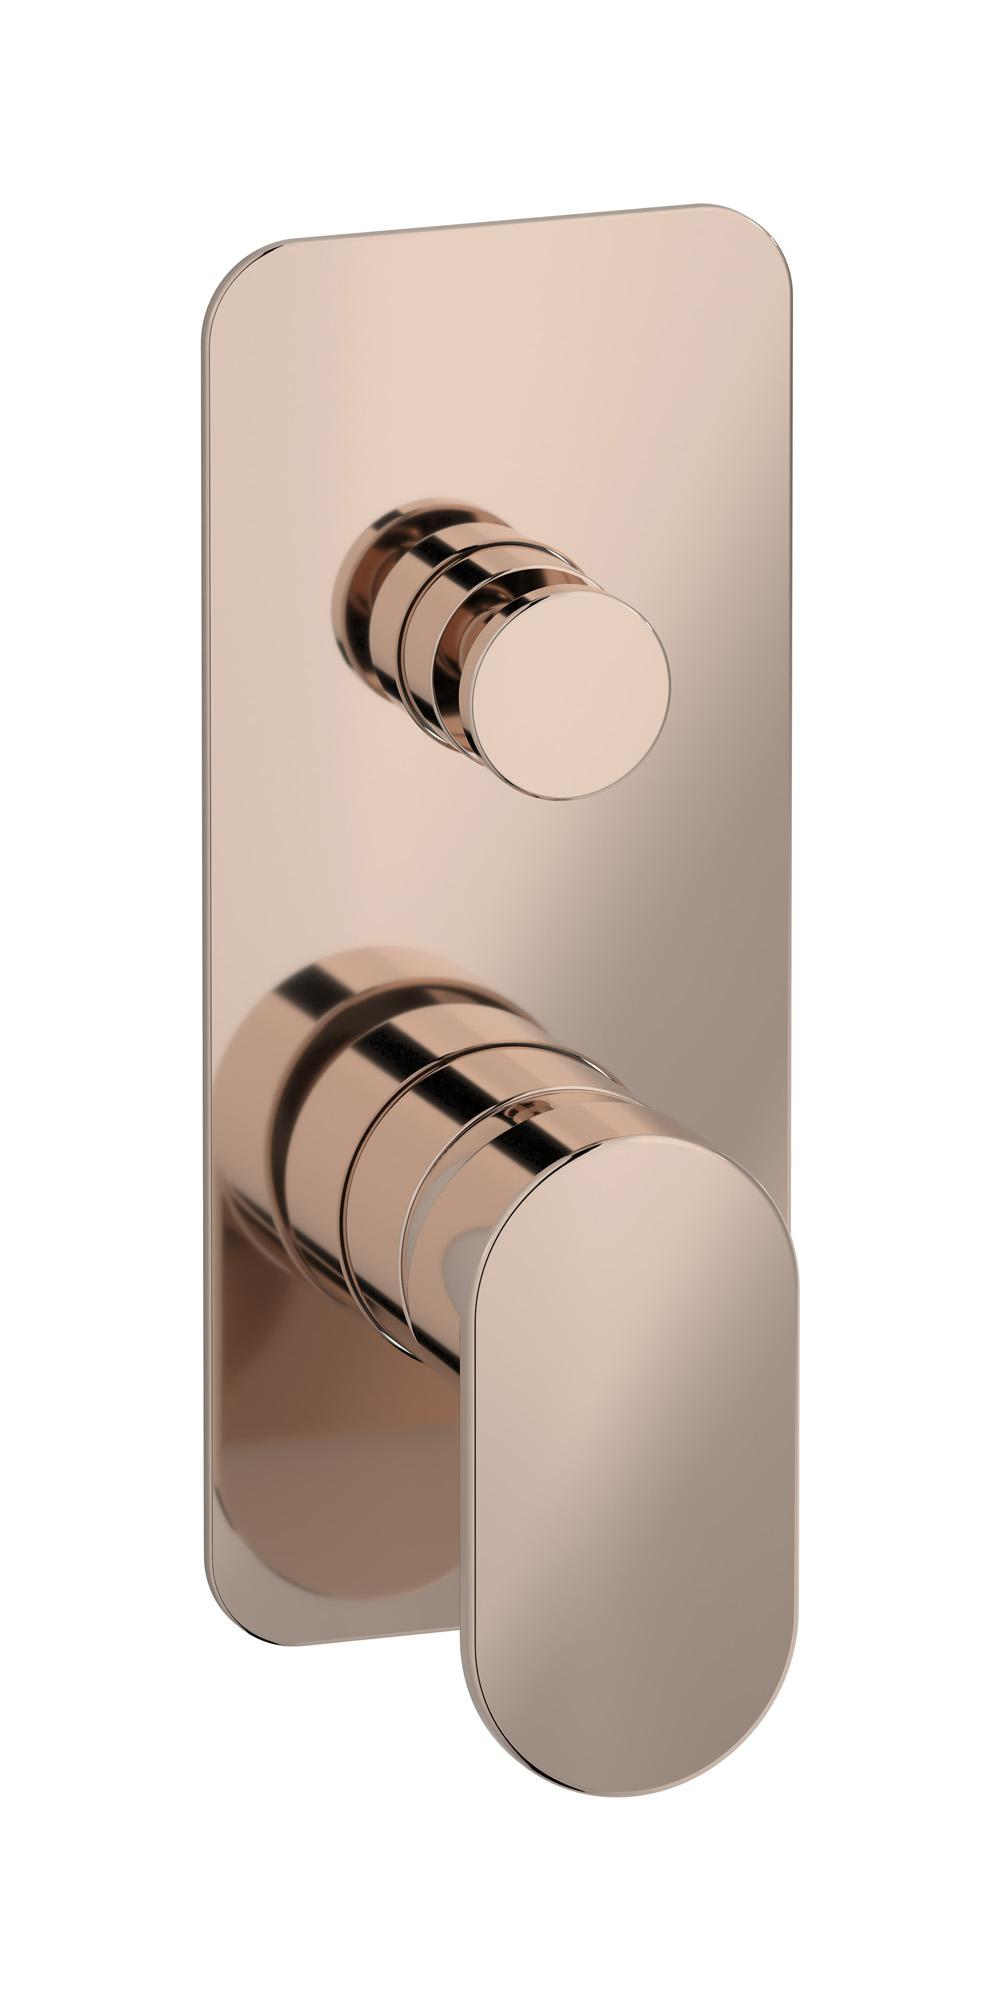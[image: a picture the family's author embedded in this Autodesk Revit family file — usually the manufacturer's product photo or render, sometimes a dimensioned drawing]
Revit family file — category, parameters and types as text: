
# Revit family: SB310
name_source: partatom
category: Apparecchi idraulici
units: mm (PartAtom-declared; Revit-internal decimal feet)

## family parameters
Basato su piano di lavoro = No
Condiviso = No
Mantieni orientamento annotazione = No
Numero OmniClass = 23.45.55.17
Punto di calcolo locali = No
Quota connettore circolare = Usa diametro
Sempre verticale = Sì
Taglio con vuoti quando caricato = No
Tipo di parte = Normale
Titolo OmniClass = Mixing Faucets

## types (6) — shared parameters
Cold water inlet = 10 mm  [stored 0.0328084 ft]
Commenti sul tipo = Wall mixer
Connessione CW = No
Connessione HW = No
Connessione di scarico = No
Connessione di ventilazione = No
Descrizione = Exposed parts for manual wall mixer with two ways diverter
Hot water inlet = 10 mm  [stored 0.0328084 ft]
Produttore = IB Rubinetterie S.p.A.
URL = https://www.weareib.it
zero-valued in all types: Prospetto di default

## per-type parameters (varying)
| type | Finishes surface | Immagine tipo | Modello |
| Chrome | IB_Chrome | SB310CC.jpg | SB310CC |
| Brushed nickel | IB_Brushed nickel | SB310SS.jpg | SB310SS |
| Matt black | IB_matt black | SB310NP.jpg | SB310NP |
| Natural brass | IB_Brass | SB310ON.jpg | SB310ON |
| Brushed gold | IB_brushed gold | SB310OS.jpg | SB310OS |
| Rose gold | IB_Rose gold | SB310RS.jpg | SB310RS |

note: [stored X ft] marks values corroborated as IEEE doubles in the binary element streams (Revit-internal decimal feet)
